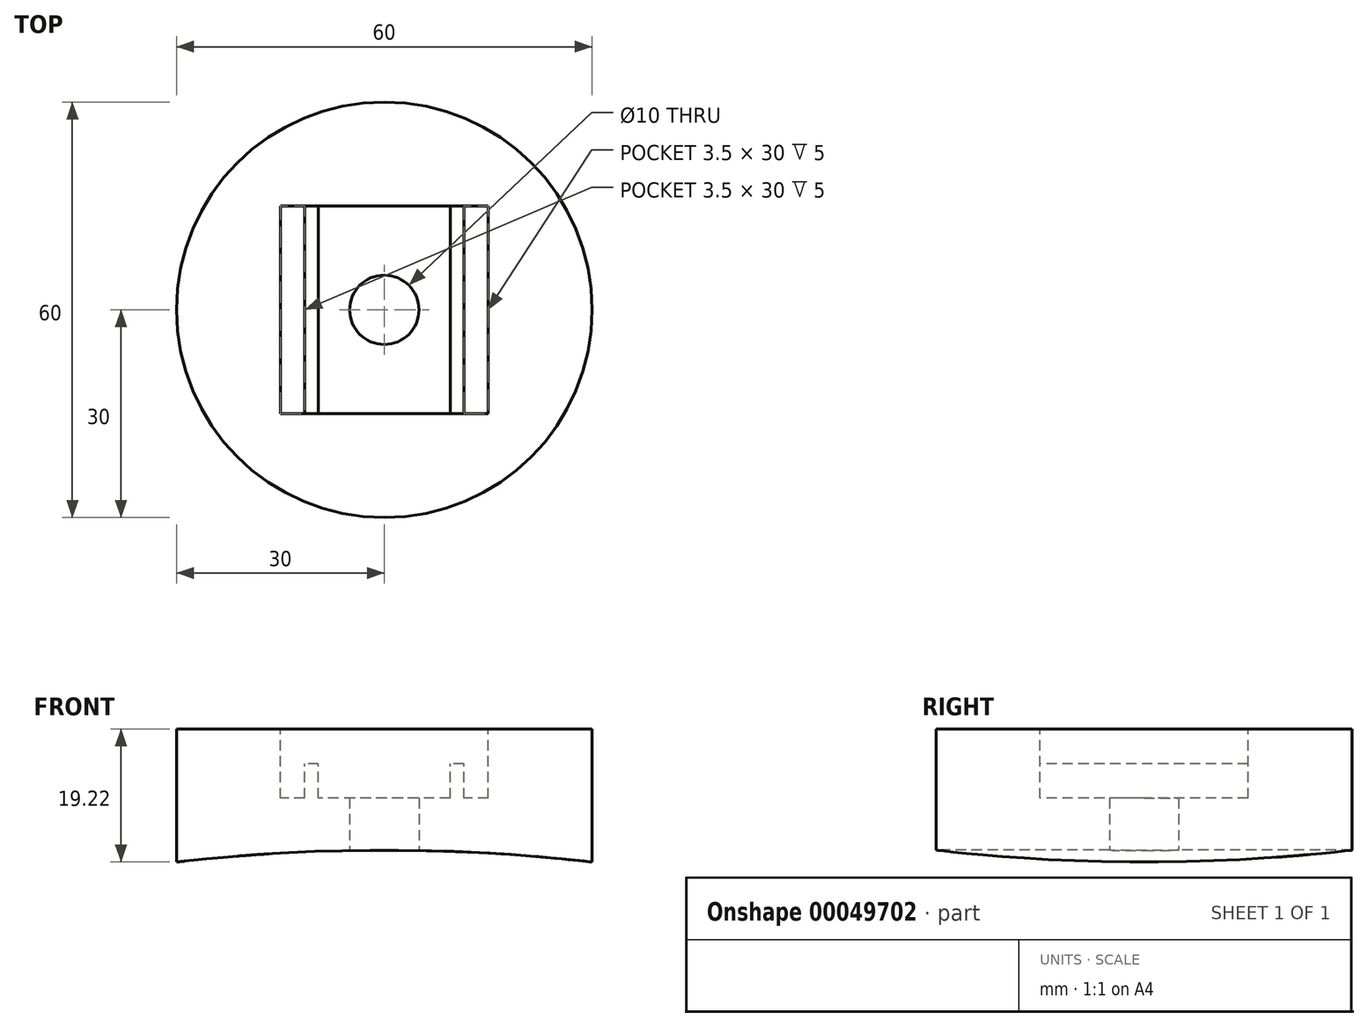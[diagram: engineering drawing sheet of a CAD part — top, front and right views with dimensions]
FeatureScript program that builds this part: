
annotation { "Feature Type Name" : "Feature", "Feature Type Description" : "" }
export const myFeature = defineFeature(function(context is Context, id is Id, definition is map)
    precondition{}
    {
        {
            var Q0;
            Q0=qCreatedBy(makeId("Top.planeOp"),FACE);
            var sketch = newSketch(context, id + "F0", { "sketchPlane" : qUnion([Q0])});
            skCircle(sketch, "E0", {"center": v(0, 0) * mm, "radius": 30 * mm});
            skCircle(sketch, "E1.0", {"center": v(0, 0) * mm, "radius": 27 * mm});
            skSolve(sketch);
        }
        {
            var Q0;
            Q0=qCreatedBy(makeId("Front.planeOp"),FACE);
            var sketch = newSketch(context, id + "F1", { "sketchPlane" : qUnion([Q0])});
            skLineSegment(sketch, "E2", {"start": v(0, 0) * mm, "end": v(0, -250) * mm});
            skCircle(sketch, "E3", {"center": v(0, -250) * mm, "radius": 262.5 * mm});
            skSolve(sketch);
        }
        {
            var Q0;
            Q0 = qSketchRegion(id + "F0", true);
            extrude(context, id + "F2", {"entities" : qUnion([Q0]), "depth" : 40 * mm, "hasSecondDirection" : true, "secondDirectionOppositeDirection" : true, "secondDirectionDepth" : 10 * mm});
        }
        {
            var Q0;
            Q0=makeQuery(id+"F0.imprint","IMPRINT",FACE,{"disambiguationData":[TD([[makeQuery(id+"F0.imprint","IMPRINT",EDGE,{"derivedFrom":sQuery(id+"F0.wireOp",EDGE,"E1.0")}),1.0]])]});
            extrude(context, id + "F3", {"entities" : qUnion([Q0]), "operationType" : NewBodyOperationType.ADD, "depth" : 25 * mm});
        }
        {
            var Q0;
            Q0=makeQuery(id+"F1.imprint","IMPRINT",FACE,{"disambiguationData":[TD([[makeQuery(id+"F1.imprint","IMPRINT",EDGE,{"derivedFrom":sQuery(id+"F1.wireOp",EDGE,"E3")}),1.0]])]});
            extrude(context, id + "F4", {"entities" : qUnion([Q0]), "operationType" : NewBodyOperationType.INTERSECT, "endBound" : BoundingType.SYMMETRIC, "oppositeDirection" : true, "depth" : 100 * mm});
        }
        {
            var Q0;
            Q0=makeQuery(id+"F0.imprint","IMPRINT",FACE,{"disambiguationData":[TD([[makeQuery(id+"F0.imprint","IMPRINT",EDGE,{"derivedFrom":sQuery(id+"F0.wireOp",EDGE,"E1.0")}),1.0]])]});
            extrude(context, id + "F5", {"entities" : qUnion([Q0]), "depth" : 30 * mm});
        }
        {
            var Q0;
            Q0=makeQuery(id+"F0.imprint","IMPRINT",FACE,{"disambiguationData":[TD([[makeQuery(id+"F0.imprint","IMPRINT",EDGE,{"derivedFrom":sQuery(id+"F0.wireOp",EDGE,"E0")}),1.0]])]});
            extrude(context, id + "F6", {"entities" : qUnion([Q0]), "operationType" : NewBodyOperationType.ADD, "depth" : 30 * mm});
        }
        {
            var Q0;
            Q0=makeQuery(id+"F1.imprint","IMPRINT",FACE,{"disambiguationData":[TD([[makeQuery(id+"F1.imprint","IMPRINT",EDGE,{"derivedFrom":sQuery(id+"F1.wireOp",EDGE,"E3")}),1.0]])]});
            extrude(context, id + "F7", {"entities" : qUnion([Q0]), "operationType" : NewBodyOperationType.REMOVE, "endBound" : BoundingType.SYMMETRIC, "oppositeDirection" : true, "depth" : 100 * mm});
        }
        {
            var Q0;
            Q0=qCreatedBy(makeId("Right.planeOp"),FACE);
            var sketch = newSketch(context, id + "F8", { "sketchPlane" : qUnion([Q0])});
            skLineSegment(sketch, "E4", {"start": v(-3.92, 0) * mm, "end": v(-3.92, -12.91) * mm});
            skLineSegment(sketch, "E5", {"start": v(3.92, 0) * mm, "end": v(3.92, -12.91) * mm});
            skLineSegment(sketch, "E6", {"start": v(3.92, -12.91) * mm, "end": v(-3.92, -12.91) * mm});
            skLineSegment(sketch, "E7", {"start": v(-3.92, 0) * mm, "end": v(3.92, 0) * mm});
            skLineSegment(sketch, "E8", {"start": v(-3.92, -1.67) * mm, "end": v(3.92, -1.67) * mm});
            skSolve(sketch);
        }
        {
            var Q0;
            {var subQ0=sQuery(id+"F8.wireOp",EDGE,"E6");Q0=makeQuery(id+"F8.imprint","IMPRINT",FACE,{"disambiguationData":[TD([[makeQuery(id+"F8.imprint","IMPRINT",EDGE,{"derivedFrom":subQ0}),-1.0]])]});}
            var Q1;
            Q1=makeQuery(id+"F2.opExtrude","SWEPT_BODY",BODY,{"disambiguationData":[OSD([sQuery(id+"F0.wireOp",EDGE,"E0"),sQuery(id+"F0.wireOp",EDGE,"E1.0")])]});
            extrude(context, id + "F9", {"entities" : qUnion([Q0]), "operationType" : NewBodyOperationType.REMOVE, "endBoundEntityBody" : qUnion([Q1]), "depth" : 50 * mm});
        }
        {
            var Q0;
            Q0=qCreatedBy(makeId("Top.planeOp"),FACE);
            var sketch = newSketch(context, id + "F10", { "sketchPlane" : qUnion([Q0])});
            skCircle(sketch, "E9", {"center": v(0, 0) * mm, "radius": 5 * mm});
            skSolve(sketch);
        }
        {
            var Q0;
            Q0 = qSketchRegion(id + "F10", true);
            extrude(context, id + "F11", {"entities" : qUnion([Q0]), "operationType" : NewBodyOperationType.REMOVE, "depth" : 50 * mm, "hasSecondDirection" : true, "secondDirectionOppositeDirection" : true, "secondDirectionDepth" : 25 * mm});
        }
        {
            var Q0;
            {var subQ0=sQuery(id+"F0.wireOp",EDGE,"E1.0");Q0=makeQuery(id+"F6.boolean.opBoolean","MERGE",FACE,{"derivedFrom":[makeQuery(id+"F5.opExtrude","CAP_FACE",FACE,{"disambiguationData":[OSD([subQ0])],"isStart":false}),makeQuery(id+"F6.opExtrude","CAP_FACE",FACE,{"disambiguationData":[OSD([sQuery(id+"F0.wireOp",EDGE,"E0"),subQ0])],"isStart":false})]});}
            var sketch = newSketch(context, id + "F12", { "sketchPlane" : qUnion([Q0])});
            skLineSegment(sketch, "E10.rect.bottom", {"start": v(15, 15) * mm, "end": v(-15, 15) * mm});
            skLineSegment(sketch, "E10.rect.top", {"start": v(15, -15) * mm, "end": v(-15, -15) * mm});
            skLineSegment(sketch, "E10.rect.left", {"start": v(15, 15) * mm, "end": v(15, -15) * mm});
            skLineSegment(sketch, "E10.rect.right", {"start": v(-15, 15) * mm, "end": v(-15, -15) * mm});
            skPoint(sketch, "E10.rect.middle", {"position": v(0, 0) * mm});
            skLineSegment(sketch, "E11", {"start": v(-11.5, 15) * mm, "end": v(-11.5, -15) * mm});
            skLineSegment(sketch, "E12", {"start": v(-9.5, 15) * mm, "end": v(-9.5, -15) * mm});
            skLineSegment(sketch, "E13", {"start": v(0, 0) * mm, "end": v(0, 15) * mm, "construction": true});
            skLineSegment(sketch, "E14.MirrorCS", {"start": v(9.5, 15) * mm, "end": v(9.5, -15) * mm});
            skLineSegment(sketch, "E15.MirrorCS", {"start": v(11.5, 15) * mm, "end": v(11.5, -15) * mm});
            skSolve(sketch);
        }
        {
            var Q0;
            {var subQ0=sQuery(id+"F12.wireOp",EDGE,"E10.rect.right");Q0=makeQuery(id+"F12.imprint","IMPRINT",FACE,{"disambiguationData":[TD([[makeQuery(id+"F12.imprint","IMPRINT",EDGE,{"derivedFrom":subQ0}),1.0]])]});}
            var Q1;
            {var subQ1=sQuery(id+"F12.wireOp",EDGE,"E12");Q1=makeQuery(id+"F12.imprint","IMPRINT",FACE,{"disambiguationData":[TD([[makeQuery(id+"F12.imprint","IMPRINT",EDGE,{"derivedFrom":subQ1}),1.0]])]});}
            var Q2;
            {var subQ0=sQuery(id+"F12.wireOp",EDGE,"E10.rect.left");Q2=makeQuery(id+"F12.imprint","IMPRINT",FACE,{"disambiguationData":[TD([[makeQuery(id+"F12.imprint","IMPRINT",EDGE,{"derivedFrom":subQ0}),-1.0]])]});}
            extrude(context, id + "F13", {"entities" : qUnion([Q0, Q1, Q2]), "operationType" : NewBodyOperationType.REMOVE, "oppositeDirection" : true, "depth" : 10 * mm});
        }
        {
            var Q0;
            {var subQ0=sQuery(id+"F12.wireOp",EDGE,"E11");Q0=makeQuery(id+"F12.imprint","IMPRINT",FACE,{"disambiguationData":[TD([[makeQuery(id+"F12.imprint","IMPRINT",EDGE,{"derivedFrom":subQ0}),1.0]])]});}
            var Q1;
            {var subQ0=sQuery(id+"F12.wireOp",EDGE,"E14.MirrorCS");Q1=makeQuery(id+"F12.imprint","IMPRINT",FACE,{"disambiguationData":[TD([[makeQuery(id+"F12.imprint","IMPRINT",EDGE,{"derivedFrom":subQ0}),1.0]])]});}
            extrude(context, id + "F14", {"entities" : qUnion([Q0, Q1]), "operationType" : NewBodyOperationType.REMOVE, "oppositeDirection" : true, "depth" : 5 * mm});
        }
    });
